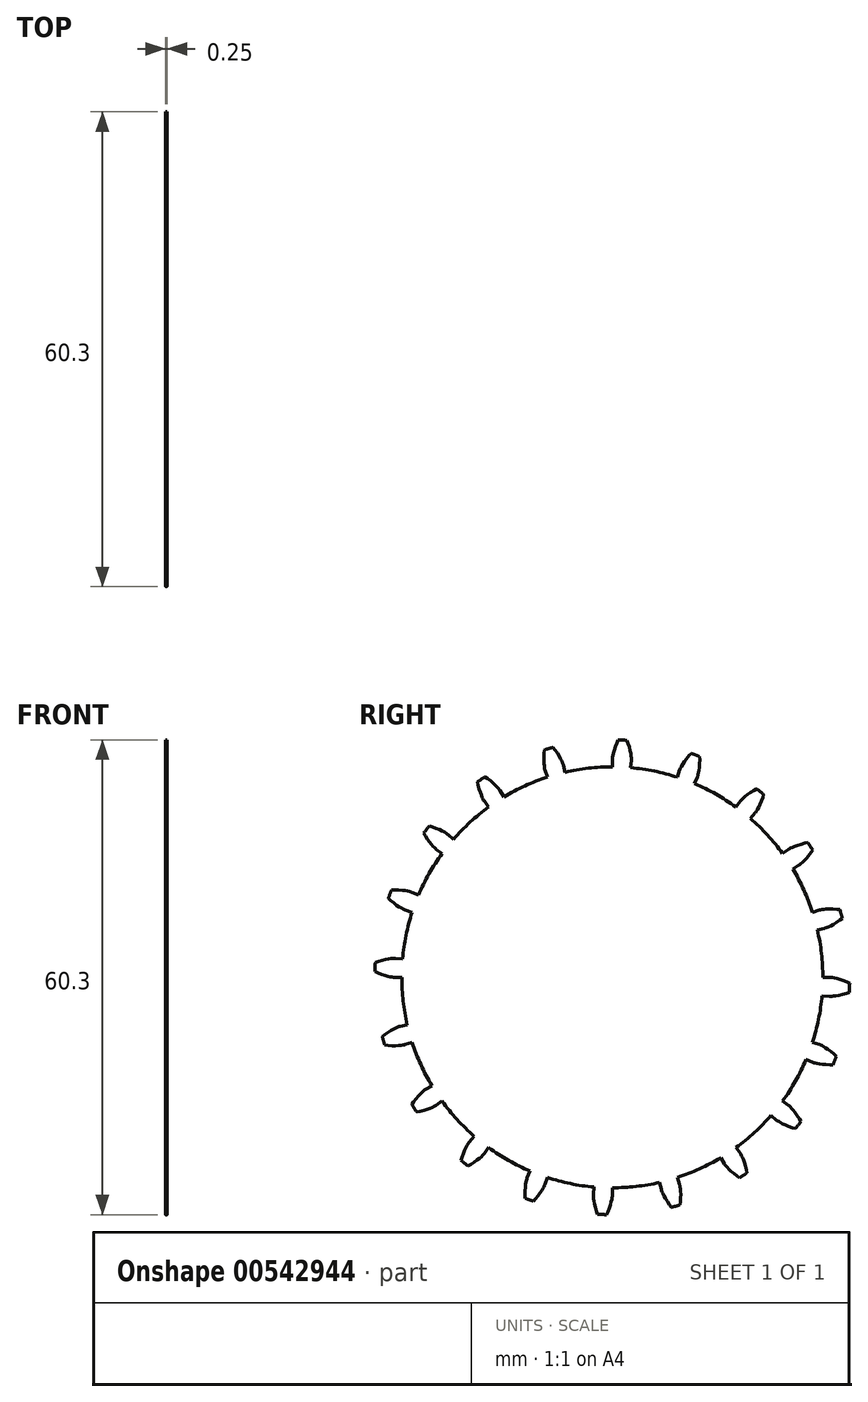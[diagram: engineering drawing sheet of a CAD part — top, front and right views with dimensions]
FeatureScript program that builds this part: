
annotation { "Feature Type Name" : "Feature", "Feature Type Description" : "" }
export const myFeature = defineFeature(function(context is Context, id is Id, definition is map)
    precondition{}
    {
        {
            assignVariable(context, id + "F0", {"name" : "GearThickness", "anyValue" : .25});
        }
        {
            var Q0;
            Q0=qCreatedBy(makeId("Right.planeOp"),FACE);
            var sketch = newSketch(context, id + "F1", { "sketchPlane" : qUnion([Q0])});
            skCircle(sketch, "E0", {"center": v(0, 0) * mm, "radius": 26.74 * mm});
            skCircle(sketch, "E1", {"center": v(0, 0) * mm, "radius": 27.66 * mm, "construction": true});
            skCircle(sketch, "E2", {"center": v(0, 0) * mm, "radius": 28.58 * mm, "construction": true});
            skCircle(sketch, "E3", {"center": v(0, 0) * mm, "radius": 30.16 * mm});
            skLineSegment(sketch, "E4", {"start": v(0, 0) * mm, "end": v(-27.66, 0) * mm, "construction": true});
            skLineSegment(sketch, "E5.1.0", {"start": v(0, 0) * mm, "end": v(-27.63, 1.38) * mm, "construction": true});
            skLineSegment(sketch, "E5.2.0", {"start": v(0, 0) * mm, "end": v(-27.53, 2.76) * mm, "construction": true});
            skLineSegment(sketch, "E5.3.0", {"start": v(0, 0) * mm, "end": v(-27.35, 4.13) * mm, "construction": true});
            skLineSegment(sketch, "E5.4.0", {"start": v(0, 0) * mm, "end": v(-27.11, 5.5) * mm, "construction": true});
            skLineSegment(sketch, "E5.5.0", {"start": v(0, 0) * mm, "end": v(-26.8, 6.84) * mm, "construction": true});
            skLineSegment(sketch, "E5.6.0", {"start": v(0, 0) * mm, "end": v(-26.43, 8.18) * mm, "construction": true});
            skLineSegment(sketch, "E5.7.0", {"start": v(0, 0) * mm, "end": v(-25.99, 9.49) * mm, "construction": true});
            skLineSegment(sketch, "E5.8.0", {"start": v(0, 0) * mm, "end": v(-25.48, 10.77) * mm, "construction": true});
            skLineSegment(sketch, "E5.9.0", {"start": v(0, 0) * mm, "end": v(-24.91, 12.03) * mm, "construction": true});
            skLineSegment(sketch, "E5.10.0", {"start": v(0, 0) * mm, "end": v(-24.28, 13.26) * mm, "construction": true});
            skLineSegment(sketch, "E5.11.0", {"start": v(0, 0) * mm, "end": v(-23.58, 14.46) * mm, "construction": true});
            skLineSegment(sketch, "E5.12.0", {"start": v(0, 0) * mm, "end": v(-22.83, 15.62) * mm, "construction": true});
            skLineSegment(sketch, "E5.13.0", {"start": v(0, 0) * mm, "end": v(-22.02, 16.74) * mm, "construction": true});
            skLineSegment(sketch, "E5.14.0", {"start": v(0, 0) * mm, "end": v(-21.16, 17.82) * mm, "construction": true});
            skLineSegment(sketch, "E5.anchor2", {"start": v(0, 0) * mm, "end": v(-21.16, 17.82) * mm, "construction": true});
            skLineSegment(sketch, "E6", {"start": v(-27.63, 1.38) * mm, "end": v(-27.7, 0) * mm, "construction": true});
            skLineSegment(sketch, "E7", {"start": v(-27.53, 2.76) * mm, "end": v(-27.8, 0) * mm, "construction": true});
            skLineSegment(sketch, "E8", {"start": v(-27.35, 4.13) * mm, "end": v(-27.97, 0.03) * mm, "construction": true});
            skLineSegment(sketch, "E9", {"start": v(-26.8, 6.84) * mm, "end": v(-28.52, 0.14) * mm, "construction": true});
            skLineSegment(sketch, "E10", {"start": v(-26.43, 8.18) * mm, "end": v(-28.88, 0.25) * mm, "construction": true});
            skLineSegment(sketch, "E11", {"start": v(-25.99, 9.49) * mm, "end": v(-29.3, 0.4) * mm, "construction": true});
            skLineSegment(sketch, "E12", {"start": v(-25.48, 10.77) * mm, "end": v(-29.8, 0.58) * mm, "construction": true});
            skLineSegment(sketch, "E13", {"start": v(-24.91, 12.03) * mm, "end": v(-30.33, 0.82) * mm, "construction": true});
            skLineSegment(sketch, "E14", {"start": v(-24.28, 13.26) * mm, "end": v(-30.9, 1.12) * mm, "construction": true});
            skLineSegment(sketch, "E15", {"start": v(-23.58, 14.46) * mm, "end": v(-31.54, 1.49) * mm, "construction": true});
            skLineSegment(sketch, "E16", {"start": v(-27.11, 5.5) * mm, "end": v(-28.21, 0.07) * mm, "construction": true});
            skLineSegment(sketch, "E17", {"start": v(-22.83, 15.62) * mm, "end": v(-32.2, 1.92) * mm, "construction": true});
            skLineSegment(sketch, "E18", {"start": v(-22.02, 16.74) * mm, "end": v(-32.9, 2.43) * mm, "construction": true});
            skLineSegment(sketch, "E19", {"start": v(-21.16, 17.82) * mm, "end": v(-33.63, 3.01) * mm, "construction": true});
            skLineSegment(sketch, "E20", {"start": v(0, 0) * mm, "end": v(-27.64, 1.2) * mm, "construction": true});
            skLineSegment(sketch, "E21", {"start": v(-26.74, 0) * mm, "end": v(-27.66, 0) * mm});
            skLineSegment(sketch, "E22.MirrorCS", {"start": v(-26.64, 2.33) * mm, "end": v(-27.56, 2.41) * mm});
            skLineSegment(sketch, "E23", {"start": v(-27.66, 0) * mm, "end": v(-27.7, 0) * mm});
            skLineSegment(sketch, "E24", {"start": v(-27.7, 0) * mm, "end": v(-27.8, 0) * mm});
            skLineSegment(sketch, "E25", {"start": v(-27.8, 0) * mm, "end": v(-27.97, 0.03) * mm});
            skLineSegment(sketch, "E26", {"start": v(-27.97, 0.03) * mm, "end": v(-28.21, 0.07) * mm});
            skLineSegment(sketch, "E27", {"start": v(-28.21, 0.07) * mm, "end": v(-28.52, 0.14) * mm});
            skLineSegment(sketch, "E28", {"start": v(-28.52, 0.14) * mm, "end": v(-28.88, 0.25) * mm});
            skLineSegment(sketch, "E29", {"start": v(-28.88, 0.25) * mm, "end": v(-29.3, 0.4) * mm});
            skLineSegment(sketch, "E30", {"start": v(-29.3, 0.4) * mm, "end": v(-29.8, 0.58) * mm});
            skLineSegment(sketch, "E31", {"start": v(-29.8, 0.58) * mm, "end": v(-30.33, 0.82) * mm});
            skLineSegment(sketch, "E32", {"start": v(-30.33, 0.82) * mm, "end": v(-30.9, 1.12) * mm});
            skLineSegment(sketch, "E33", {"start": v(-30.9, 1.12) * mm, "end": v(-31.54, 1.49) * mm});
            skLineSegment(sketch, "E34", {"start": v(-31.54, 1.49) * mm, "end": v(-32.2, 1.92) * mm});
            skLineSegment(sketch, "E35", {"start": v(-32.2, 1.92) * mm, "end": v(-32.9, 2.43) * mm});
            skLineSegment(sketch, "E36", {"start": v(-32.9, 2.43) * mm, "end": v(-33.63, 3.01) * mm});
            skLineSegment(sketch, "E37.MirrorCS", {"start": v(-27.56, 2.41) * mm, "end": v(-27.6, 2.41) * mm});
            skLineSegment(sketch, "E38.MirrorCS", {"start": v(-27.6, 2.41) * mm, "end": v(-27.7, 2.41) * mm});
            skLineSegment(sketch, "E39.MirrorCS", {"start": v(-27.7, 2.41) * mm, "end": v(-27.87, 2.4) * mm});
            skLineSegment(sketch, "E40.MirrorCS", {"start": v(-27.87, 2.4) * mm, "end": v(-28.11, 2.39) * mm});
            skLineSegment(sketch, "E41.MirrorCS", {"start": v(-28.42, 2.34) * mm, "end": v(-28.8, 2.27) * mm});
            skLineSegment(sketch, "E42.MirrorCS", {"start": v(-28.8, 2.27) * mm, "end": v(-29.23, 2.17) * mm});
            skLineSegment(sketch, "E43.MirrorCS", {"start": v(-29.23, 2.17) * mm, "end": v(-29.73, 2.02) * mm});
            skLineSegment(sketch, "E44.MirrorCS", {"start": v(-29.73, 2.02) * mm, "end": v(-30.28, 1.82) * mm});
            skLineSegment(sketch, "E45.MirrorCS", {"start": v(-30.9, 1.57) * mm, "end": v(-31.55, 1.27) * mm});
            skLineSegment(sketch, "E46.MirrorCS", {"start": v(-30.28, 1.82) * mm, "end": v(-30.9, 1.57) * mm});
            skLineSegment(sketch, "E47.MirrorCS", {"start": v(-31.55, 1.27) * mm, "end": v(-32.25, 0.9) * mm});
            skLineSegment(sketch, "E48.MirrorCS", {"start": v(-32.25, 0.9) * mm, "end": v(-33, 0.45) * mm});
            skLineSegment(sketch, "E49.MirrorCS", {"start": v(-33, 0.45) * mm, "end": v(-33.77, -0.07) * mm});
            skLineSegment(sketch, "E50.MirrorCS", {"start": v(-28.11, 2.39) * mm, "end": v(-28.42, 2.34) * mm});
            skLineSegment(sketch, "E51.1.0", {"start": v(-25.43, -8.26) * mm, "end": v(-26.31, -8.55) * mm});
            skLineSegment(sketch, "E51.1.1", {"start": v(-30.4, -8.54) * mm, "end": v(-30.95, -9.12) * mm});
            skLineSegment(sketch, "E51.1.2", {"start": v(-26.05, -6.01) * mm, "end": v(-26.96, -6.22) * mm});
            skLineSegment(sketch, "E51.1.3", {"start": v(-29.86, -8.05) * mm, "end": v(-30.4, -8.54) * mm});
            skLineSegment(sketch, "E51.1.4", {"start": v(-29.74, -8.48) * mm, "end": v(-30.45, -8.33) * mm});
            skLineSegment(sketch, "E51.1.5", {"start": v(-30.45, -8.33) * mm, "end": v(-31.22, -8.12) * mm});
            skLineSegment(sketch, "E51.1.6", {"start": v(-29.36, -7.62) * mm, "end": v(-29.86, -8.05) * mm});
            skLineSegment(sketch, "E51.1.7", {"start": v(-31.52, -9.77) * mm, "end": v(-32.1, -10.5) * mm});
            skLineSegment(sketch, "E51.1.8", {"start": v(-28.9, -7.27) * mm, "end": v(-29.36, -7.62) * mm});
            skLineSegment(sketch, "E51.1.9", {"start": v(-32.05, -7.86) * mm, "end": v(-32.92, -7.53) * mm});
            skLineSegment(sketch, "E51.1.10", {"start": v(-30.95, -9.12) * mm, "end": v(-31.52, -9.77) * mm});
            skLineSegment(sketch, "E51.1.11", {"start": v(-29.1, -8.59) * mm, "end": v(-29.74, -8.48) * mm});
            skLineSegment(sketch, "E51.1.12", {"start": v(-31.22, -8.12) * mm, "end": v(-32.05, -7.86) * mm});
            skLineSegment(sketch, "E51.1.13", {"start": v(-27.75, -6.55) * mm, "end": v(-28.09, -6.74) * mm});
            skLineSegment(sketch, "E51.1.14", {"start": v(-28.09, -6.74) * mm, "end": v(-28.47, -6.97) * mm});
            skLineSegment(sketch, "E51.1.15", {"start": v(-28.47, -6.97) * mm, "end": v(-28.9, -7.27) * mm});
            skLineSegment(sketch, "E51.1.16", {"start": v(-28, -8.69) * mm, "end": v(-28.51, -8.65) * mm});
            skLineSegment(sketch, "E51.1.17", {"start": v(-27.54, -8.7) * mm, "end": v(-28, -8.69) * mm});
            skLineSegment(sketch, "E51.1.18", {"start": v(-28.51, -8.65) * mm, "end": v(-29.1, -8.59) * mm});
            skLineSegment(sketch, "E51.1.19", {"start": v(-27.47, -6.42) * mm, "end": v(-27.75, -6.55) * mm});
            skLineSegment(sketch, "E51.1.20", {"start": v(-27.25, -6.32) * mm, "end": v(-27.47, -6.42) * mm});
            skLineSegment(sketch, "E51.1.21", {"start": v(-27.16, -8.68) * mm, "end": v(-27.54, -8.7) * mm});
            skLineSegment(sketch, "E51.1.22", {"start": v(-26.85, -8.65) * mm, "end": v(-27.16, -8.68) * mm});
            skLineSegment(sketch, "E51.1.23", {"start": v(-26.44, -8.58) * mm, "end": v(-26.61, -8.62) * mm});
            skLineSegment(sketch, "E51.1.24", {"start": v(-26.96, -6.22) * mm, "end": v(-26.99, -6.23) * mm});
            skLineSegment(sketch, "E51.1.25", {"start": v(-26.99, -6.23) * mm, "end": v(-27.09, -6.26) * mm});
            skLineSegment(sketch, "E51.1.26", {"start": v(-26.61, -8.62) * mm, "end": v(-26.85, -8.65) * mm});
            skLineSegment(sketch, "E51.1.27", {"start": v(-27.09, -6.26) * mm, "end": v(-27.25, -6.32) * mm});
            skLineSegment(sketch, "E51.1.28", {"start": v(-26.34, -8.56) * mm, "end": v(-26.44, -8.58) * mm});
            skLineSegment(sketch, "E51.1.29", {"start": v(-26.31, -8.55) * mm, "end": v(-26.34, -8.56) * mm});
            skLineSegment(sketch, "E51.2.0", {"start": v(-21.63, -15.72) * mm, "end": v(-22.38, -16.26) * mm});
            skLineSegment(sketch, "E51.2.1", {"start": v(-26.27, -17.52) * mm, "end": v(-26.62, -18.23) * mm});
            skLineSegment(sketch, "E51.2.2", {"start": v(-22.92, -13.77) * mm, "end": v(-23.71, -14.25) * mm});
            skLineSegment(sketch, "E51.2.3", {"start": v(-25.92, -16.88) * mm, "end": v(-26.27, -17.52) * mm});
            skLineSegment(sketch, "E51.2.4", {"start": v(-25.67, -17.26) * mm, "end": v(-26.39, -17.33) * mm});
            skLineSegment(sketch, "E51.2.5", {"start": v(-26.39, -17.33) * mm, "end": v(-27.18, -17.38) * mm});
            skLineSegment(sketch, "E51.2.6", {"start": v(-25.57, -16.32) * mm, "end": v(-25.92, -16.88) * mm});
            skLineSegment(sketch, "E51.2.7", {"start": v(-26.96, -19.03) * mm, "end": v(-27.28, -19.9) * mm});
            skLineSegment(sketch, "E51.2.8", {"start": v(-25.24, -15.84) * mm, "end": v(-25.57, -16.32) * mm});
            skLineSegment(sketch, "E51.2.9", {"start": v(-28.05, -17.38) * mm, "end": v(-28.98, -17.33) * mm});
            skLineSegment(sketch, "E51.2.10", {"start": v(-26.62, -18.23) * mm, "end": v(-26.96, -19.03) * mm});
            skLineSegment(sketch, "E51.2.11", {"start": v(-25.02, -17.16) * mm, "end": v(-25.67, -17.26) * mm});
            skLineSegment(sketch, "E51.2.12", {"start": v(-27.18, -17.38) * mm, "end": v(-28.05, -17.38) * mm});
            skLineSegment(sketch, "E51.2.13", {"start": v(-24.37, -14.8) * mm, "end": v(-24.63, -15.09) * mm});
            skLineSegment(sketch, "E51.2.14", {"start": v(-24.63, -15.09) * mm, "end": v(-24.92, -15.43) * mm});
            skLineSegment(sketch, "E51.2.15", {"start": v(-24.92, -15.43) * mm, "end": v(-25.24, -15.84) * mm});
            skLineSegment(sketch, "E51.2.16", {"start": v(-23.94, -16.91) * mm, "end": v(-24.44, -17.04) * mm});
            skLineSegment(sketch, "E51.2.17", {"start": v(-23.51, -16.78) * mm, "end": v(-23.94, -16.91) * mm});
            skLineSegment(sketch, "E51.2.18", {"start": v(-24.44, -17.04) * mm, "end": v(-25.02, -17.16) * mm});
            skLineSegment(sketch, "E51.2.19", {"start": v(-24.15, -14.6) * mm, "end": v(-24.37, -14.8) * mm});
            skLineSegment(sketch, "E51.2.20", {"start": v(-23.96, -14.43) * mm, "end": v(-24.15, -14.6) * mm});
            skLineSegment(sketch, "E51.2.21", {"start": v(-23.15, -16.65) * mm, "end": v(-23.51, -16.78) * mm});
            skLineSegment(sketch, "E51.2.22", {"start": v(-22.87, -16.52) * mm, "end": v(-23.15, -16.65) * mm});
            skLineSegment(sketch, "E51.2.23", {"start": v(-22.5, -16.33) * mm, "end": v(-22.65, -16.42) * mm});
            skLineSegment(sketch, "E51.2.24", {"start": v(-23.71, -14.25) * mm, "end": v(-23.74, -14.27) * mm});
            skLineSegment(sketch, "E51.2.25", {"start": v(-23.74, -14.27) * mm, "end": v(-23.83, -14.33) * mm});
            skLineSegment(sketch, "E51.2.26", {"start": v(-22.65, -16.42) * mm, "end": v(-22.87, -16.52) * mm});
            skLineSegment(sketch, "E51.2.27", {"start": v(-23.83, -14.33) * mm, "end": v(-23.96, -14.43) * mm});
            skLineSegment(sketch, "E51.2.28", {"start": v(-22.4, -16.28) * mm, "end": v(-22.5, -16.33) * mm});
            skLineSegment(sketch, "E51.2.29", {"start": v(-22.38, -16.26) * mm, "end": v(-22.4, -16.28) * mm});
            skLineSegment(sketch, "E51.3.0", {"start": v(-15.72, -21.63) * mm, "end": v(-16.26, -22.38) * mm});
            skLineSegment(sketch, "E51.3.1", {"start": v(-19.57, -24.78) * mm, "end": v(-19.68, -25.57) * mm});
            skLineSegment(sketch, "E51.3.2", {"start": v(-17.54, -20.18) * mm, "end": v(-18.15, -20.88) * mm});
            skLineSegment(sketch, "E51.3.3", {"start": v(-19.43, -24.07) * mm, "end": v(-19.57, -24.78) * mm});
            skLineSegment(sketch, "E51.3.4", {"start": v(-19.08, -24.35) * mm, "end": v(-19.74, -24.64) * mm});
            skLineSegment(sketch, "E51.3.5", {"start": v(-19.74, -24.64) * mm, "end": v(-20.48, -24.93) * mm});
            skLineSegment(sketch, "E51.3.6", {"start": v(-19.27, -23.43) * mm, "end": v(-19.43, -24.07) * mm});
            skLineSegment(sketch, "E51.3.7", {"start": v(-19.76, -26.43) * mm, "end": v(-19.8, -27.36) * mm});
            skLineSegment(sketch, "E51.3.8", {"start": v(-19.1, -22.86) * mm, "end": v(-19.27, -23.43) * mm});
            skLineSegment(sketch, "E51.3.9", {"start": v(-21.3, -25.2) * mm, "end": v(-22.2, -25.44) * mm});
            skLineSegment(sketch, "E51.3.10", {"start": v(-19.68, -25.57) * mm, "end": v(-19.76, -26.43) * mm});
            skLineSegment(sketch, "E51.3.11", {"start": v(-18.5, -24.05) * mm, "end": v(-19.08, -24.35) * mm});
            skLineSegment(sketch, "E51.3.12", {"start": v(-20.48, -24.93) * mm, "end": v(-21.3, -25.2) * mm});
            skLineSegment(sketch, "E51.3.13", {"start": v(-18.6, -21.62) * mm, "end": v(-18.76, -21.96) * mm});
            skLineSegment(sketch, "E51.3.14", {"start": v(-18.76, -21.96) * mm, "end": v(-18.93, -22.38) * mm});
            skLineSegment(sketch, "E51.3.15", {"start": v(-18.93, -22.38) * mm, "end": v(-19.1, -22.86) * mm});
            skLineSegment(sketch, "E51.3.16", {"start": v(-17.54, -23.48) * mm, "end": v(-17.98, -23.76) * mm});
            skLineSegment(sketch, "E51.3.17", {"start": v(-17.18, -23.22) * mm, "end": v(-17.54, -23.48) * mm});
            skLineSegment(sketch, "E51.3.18", {"start": v(-17.98, -23.76) * mm, "end": v(-18.5, -24.05) * mm});
            skLineSegment(sketch, "E51.3.19", {"start": v(-18.45, -21.34) * mm, "end": v(-18.6, -21.62) * mm});
            skLineSegment(sketch, "E51.3.20", {"start": v(-18.33, -21.13) * mm, "end": v(-18.45, -21.34) * mm});
            skLineSegment(sketch, "E51.3.21", {"start": v(-16.88, -22.99) * mm, "end": v(-17.18, -23.22) * mm});
            skLineSegment(sketch, "E51.3.22", {"start": v(-16.64, -22.78) * mm, "end": v(-16.88, -22.99) * mm});
            skLineSegment(sketch, "E51.3.23", {"start": v(-16.35, -22.49) * mm, "end": v(-16.47, -22.61) * mm});
            skLineSegment(sketch, "E51.3.24", {"start": v(-18.15, -20.88) * mm, "end": v(-18.17, -20.9) * mm});
            skLineSegment(sketch, "E51.3.25", {"start": v(-18.17, -20.9) * mm, "end": v(-18.23, -20.99) * mm});
            skLineSegment(sketch, "E51.3.26", {"start": v(-16.47, -22.61) * mm, "end": v(-16.64, -22.78) * mm});
            skLineSegment(sketch, "E51.3.27", {"start": v(-18.23, -20.99) * mm, "end": v(-18.33, -21.13) * mm});
            skLineSegment(sketch, "E51.3.28", {"start": v(-16.28, -22.4) * mm, "end": v(-16.35, -22.49) * mm});
            skLineSegment(sketch, "E51.3.29", {"start": v(-16.26, -22.38) * mm, "end": v(-16.28, -22.4) * mm});
            skLineSegment(sketch, "E51.4.0", {"start": v(-8.26, -25.43) * mm, "end": v(-8.55, -26.31) * mm});
            skLineSegment(sketch, "E51.4.1", {"start": v(-10.95, -29.61) * mm, "end": v(-10.82, -30.4) * mm});
            skLineSegment(sketch, "E51.4.2", {"start": v(-10.45, -24.61) * mm, "end": v(-10.8, -25.47) * mm});
            skLineSegment(sketch, "E51.4.3", {"start": v(-11.04, -28.9) * mm, "end": v(-10.95, -29.61) * mm});
            skLineSegment(sketch, "E51.4.4", {"start": v(-10.62, -29.05) * mm, "end": v(-11.16, -29.53) * mm});
            skLineSegment(sketch, "E51.4.5", {"start": v(-11.16, -29.53) * mm, "end": v(-11.78, -30.04) * mm});
            skLineSegment(sketch, "E51.4.6", {"start": v(-11.1, -28.24) * mm, "end": v(-11.04, -28.9) * mm});
            skLineSegment(sketch, "E51.4.7", {"start": v(-10.62, -31.24) * mm, "end": v(-10.37, -32.14) * mm});
            skLineSegment(sketch, "E51.4.8", {"start": v(-11.1, -27.65) * mm, "end": v(-11.1, -28.24) * mm});
            skLineSegment(sketch, "E51.4.9", {"start": v(-12.48, -30.55) * mm, "end": v(-13.26, -31.06) * mm});
            skLineSegment(sketch, "E51.4.10", {"start": v(-10.82, -30.4) * mm, "end": v(-10.62, -31.24) * mm});
            skLineSegment(sketch, "E51.4.11", {"start": v(-10.15, -28.59) * mm, "end": v(-10.62, -29.05) * mm});
            skLineSegment(sketch, "E51.4.12", {"start": v(-11.78, -30.04) * mm, "end": v(-12.48, -30.55) * mm});
            skLineSegment(sketch, "E51.4.13", {"start": v(-11.01, -26.3) * mm, "end": v(-11.06, -26.68) * mm});
            skLineSegment(sketch, "E51.4.14", {"start": v(-11.06, -26.68) * mm, "end": v(-11.1, -27.13) * mm});
            skLineSegment(sketch, "E51.4.15", {"start": v(-11.1, -27.13) * mm, "end": v(-11.1, -27.65) * mm});
            skLineSegment(sketch, "E51.4.16", {"start": v(-9.43, -27.75) * mm, "end": v(-9.76, -28.15) * mm});
            skLineSegment(sketch, "E51.4.17", {"start": v(-9.16, -27.4) * mm, "end": v(-9.43, -27.75) * mm});
            skLineSegment(sketch, "E51.4.18", {"start": v(-9.76, -28.15) * mm, "end": v(-10.15, -28.59) * mm});
            skLineSegment(sketch, "E51.4.19", {"start": v(-10.96, -26) * mm, "end": v(-11.01, -26.3) * mm});
            skLineSegment(sketch, "E51.4.20", {"start": v(-10.9, -25.76) * mm, "end": v(-10.96, -26) * mm});
            skLineSegment(sketch, "E51.4.21", {"start": v(-8.95, -27.08) * mm, "end": v(-9.16, -27.4) * mm});
            skLineSegment(sketch, "E51.4.22", {"start": v(-8.79, -26.8) * mm, "end": v(-8.95, -27.08) * mm});
            skLineSegment(sketch, "E51.4.23", {"start": v(-8.6, -26.44) * mm, "end": v(-8.67, -26.6) * mm});
            skLineSegment(sketch, "E51.4.24", {"start": v(-10.8, -25.47) * mm, "end": v(-10.82, -25.5) * mm});
            skLineSegment(sketch, "E51.4.25", {"start": v(-10.82, -25.5) * mm, "end": v(-10.85, -25.6) * mm});
            skLineSegment(sketch, "E51.4.26", {"start": v(-8.67, -26.6) * mm, "end": v(-8.79, -26.8) * mm});
            skLineSegment(sketch, "E51.4.27", {"start": v(-10.85, -25.6) * mm, "end": v(-10.9, -25.76) * mm});
            skLineSegment(sketch, "E51.4.28", {"start": v(-8.56, -26.34) * mm, "end": v(-8.6, -26.44) * mm});
            skLineSegment(sketch, "E51.4.29", {"start": v(-8.55, -26.31) * mm, "end": v(-8.56, -26.34) * mm});
            skLineSegment(sketch, "E51.5.0", {"start": v(0, -26.74) * mm, "end": v(0, -27.66) * mm});
            skLineSegment(sketch, "E51.5.1", {"start": v(-1.27, -31.55) * mm, "end": v(-0.9, -32.25) * mm});
            skLineSegment(sketch, "E51.5.2", {"start": v(-2.33, -26.64) * mm, "end": v(-2.41, -27.56) * mm});
            skLineSegment(sketch, "E51.5.3", {"start": v(-1.57, -30.9) * mm, "end": v(-1.27, -31.55) * mm});
            skLineSegment(sketch, "E51.5.4", {"start": v(-1.12, -30.9) * mm, "end": v(-1.49, -31.54) * mm});
            skLineSegment(sketch, "E51.5.5", {"start": v(-1.49, -31.54) * mm, "end": v(-1.92, -32.2) * mm});
            skLineSegment(sketch, "E51.5.6", {"start": v(-1.82, -30.28) * mm, "end": v(-1.57, -30.9) * mm});
            skLineSegment(sketch, "E51.5.7", {"start": v(-0.45, -33) * mm, "end": v(0.07, -33.77) * mm});
            skLineSegment(sketch, "E51.5.8", {"start": v(-2.02, -29.73) * mm, "end": v(-1.82, -30.28) * mm});
            skLineSegment(sketch, "E51.5.9", {"start": v(-2.43, -32.9) * mm, "end": v(-3.01, -33.63) * mm});
            skLineSegment(sketch, "E51.5.10", {"start": v(-0.9, -32.25) * mm, "end": v(-0.45, -33) * mm});
            skLineSegment(sketch, "E51.5.11", {"start": v(-0.82, -30.33) * mm, "end": v(-1.12, -30.9) * mm});
            skLineSegment(sketch, "E51.5.12", {"start": v(-1.92, -32.2) * mm, "end": v(-2.43, -32.9) * mm});
            skLineSegment(sketch, "E51.5.13", {"start": v(-2.34, -28.42) * mm, "end": v(-2.27, -28.8) * mm});
            skLineSegment(sketch, "E51.5.14", {"start": v(-2.27, -28.8) * mm, "end": v(-2.17, -29.23) * mm});
            skLineSegment(sketch, "E51.5.15", {"start": v(-2.17, -29.23) * mm, "end": v(-2.02, -29.73) * mm});
            skLineSegment(sketch, "E51.5.16", {"start": v(-0.4, -29.3) * mm, "end": v(-0.58, -29.8) * mm});
            skLineSegment(sketch, "E51.5.17", {"start": v(-0.25, -28.88) * mm, "end": v(-0.4, -29.3) * mm});
            skLineSegment(sketch, "E51.5.18", {"start": v(-0.58, -29.8) * mm, "end": v(-0.82, -30.33) * mm});
            skLineSegment(sketch, "E51.5.19", {"start": v(-2.39, -28.11) * mm, "end": v(-2.34, -28.42) * mm});
            skLineSegment(sketch, "E51.5.20", {"start": v(-2.4, -27.87) * mm, "end": v(-2.39, -28.11) * mm});
            skLineSegment(sketch, "E51.5.21", {"start": v(-0.14, -28.52) * mm, "end": v(-0.25, -28.88) * mm});
            skLineSegment(sketch, "E51.5.22", {"start": v(-0.07, -28.21) * mm, "end": v(-0.14, -28.52) * mm});
            skLineSegment(sketch, "E51.5.23", {"start": v(0, -27.8) * mm, "end": v(-0.03, -27.97) * mm});
            skLineSegment(sketch, "E51.5.24", {"start": v(-2.41, -27.56) * mm, "end": v(-2.41, -27.6) * mm});
            skLineSegment(sketch, "E51.5.25", {"start": v(-2.41, -27.6) * mm, "end": v(-2.41, -27.7) * mm});
            skLineSegment(sketch, "E51.5.26", {"start": v(-0.03, -27.97) * mm, "end": v(-0.07, -28.21) * mm});
            skLineSegment(sketch, "E51.5.27", {"start": v(-2.41, -27.7) * mm, "end": v(-2.4, -27.87) * mm});
            skLineSegment(sketch, "E51.5.28", {"start": v(0, -27.7) * mm, "end": v(0, -27.8) * mm});
            skLineSegment(sketch, "E51.5.29", {"start": v(0, -27.66) * mm, "end": v(0, -27.7) * mm});
            skLineSegment(sketch, "E51.6.0", {"start": v(8.26, -25.43) * mm, "end": v(8.55, -26.31) * mm});
            skLineSegment(sketch, "E51.6.1", {"start": v(8.54, -30.4) * mm, "end": v(9.12, -30.95) * mm});
            skLineSegment(sketch, "E51.6.2", {"start": v(6.01, -26.05) * mm, "end": v(6.22, -26.96) * mm});
            skLineSegment(sketch, "E51.6.3", {"start": v(8.05, -29.86) * mm, "end": v(8.54, -30.4) * mm});
            skLineSegment(sketch, "E51.6.4", {"start": v(8.48, -29.74) * mm, "end": v(8.33, -30.45) * mm});
            skLineSegment(sketch, "E51.6.5", {"start": v(8.33, -30.45) * mm, "end": v(8.12, -31.22) * mm});
            skLineSegment(sketch, "E51.6.6", {"start": v(7.62, -29.36) * mm, "end": v(8.05, -29.86) * mm});
            skLineSegment(sketch, "E51.6.7", {"start": v(9.77, -31.52) * mm, "end": v(10.5, -32.1) * mm});
            skLineSegment(sketch, "E51.6.8", {"start": v(7.27, -28.9) * mm, "end": v(7.62, -29.36) * mm});
            skLineSegment(sketch, "E51.6.9", {"start": v(7.86, -32.05) * mm, "end": v(7.53, -32.92) * mm});
            skLineSegment(sketch, "E51.6.10", {"start": v(9.12, -30.95) * mm, "end": v(9.77, -31.52) * mm});
            skLineSegment(sketch, "E51.6.11", {"start": v(8.59, -29.1) * mm, "end": v(8.48, -29.74) * mm});
            skLineSegment(sketch, "E51.6.12", {"start": v(8.12, -31.22) * mm, "end": v(7.86, -32.05) * mm});
            skLineSegment(sketch, "E51.6.13", {"start": v(6.55, -27.75) * mm, "end": v(6.74, -28.09) * mm});
            skLineSegment(sketch, "E51.6.14", {"start": v(6.74, -28.09) * mm, "end": v(6.97, -28.47) * mm});
            skLineSegment(sketch, "E51.6.15", {"start": v(6.97, -28.47) * mm, "end": v(7.27, -28.9) * mm});
            skLineSegment(sketch, "E51.6.16", {"start": v(8.69, -28) * mm, "end": v(8.65, -28.51) * mm});
            skLineSegment(sketch, "E51.6.17", {"start": v(8.7, -27.54) * mm, "end": v(8.69, -28) * mm});
            skLineSegment(sketch, "E51.6.18", {"start": v(8.65, -28.51) * mm, "end": v(8.59, -29.1) * mm});
            skLineSegment(sketch, "E51.6.19", {"start": v(6.42, -27.47) * mm, "end": v(6.55, -27.75) * mm});
            skLineSegment(sketch, "E51.6.20", {"start": v(6.32, -27.25) * mm, "end": v(6.42, -27.47) * mm});
            skLineSegment(sketch, "E51.6.21", {"start": v(8.68, -27.16) * mm, "end": v(8.7, -27.54) * mm});
            skLineSegment(sketch, "E51.6.22", {"start": v(8.65, -26.85) * mm, "end": v(8.68, -27.16) * mm});
            skLineSegment(sketch, "E51.6.23", {"start": v(8.58, -26.44) * mm, "end": v(8.62, -26.61) * mm});
            skLineSegment(sketch, "E51.6.24", {"start": v(6.22, -26.96) * mm, "end": v(6.23, -26.99) * mm});
            skLineSegment(sketch, "E51.6.25", {"start": v(6.23, -26.99) * mm, "end": v(6.26, -27.09) * mm});
            skLineSegment(sketch, "E51.6.26", {"start": v(8.62, -26.61) * mm, "end": v(8.65, -26.85) * mm});
            skLineSegment(sketch, "E51.6.27", {"start": v(6.26, -27.09) * mm, "end": v(6.32, -27.25) * mm});
            skLineSegment(sketch, "E51.6.28", {"start": v(8.56, -26.34) * mm, "end": v(8.58, -26.44) * mm});
            skLineSegment(sketch, "E51.6.29", {"start": v(8.55, -26.31) * mm, "end": v(8.56, -26.34) * mm});
            skLineSegment(sketch, "E51.7.0", {"start": v(15.72, -21.63) * mm, "end": v(16.26, -22.38) * mm});
            skLineSegment(sketch, "E51.7.1", {"start": v(17.52, -26.27) * mm, "end": v(18.23, -26.62) * mm});
            skLineSegment(sketch, "E51.7.2", {"start": v(13.77, -22.92) * mm, "end": v(14.25, -23.71) * mm});
            skLineSegment(sketch, "E51.7.3", {"start": v(16.88, -25.92) * mm, "end": v(17.52, -26.27) * mm});
            skLineSegment(sketch, "E51.7.4", {"start": v(17.26, -25.67) * mm, "end": v(17.33, -26.39) * mm});
            skLineSegment(sketch, "E51.7.5", {"start": v(17.33, -26.39) * mm, "end": v(17.38, -27.18) * mm});
            skLineSegment(sketch, "E51.7.6", {"start": v(16.32, -25.57) * mm, "end": v(16.88, -25.92) * mm});
            skLineSegment(sketch, "E51.7.7", {"start": v(19.03, -26.96) * mm, "end": v(19.9, -27.28) * mm});
            skLineSegment(sketch, "E51.7.8", {"start": v(15.84, -25.24) * mm, "end": v(16.32, -25.57) * mm});
            skLineSegment(sketch, "E51.7.9", {"start": v(17.38, -28.05) * mm, "end": v(17.33, -28.98) * mm});
            skLineSegment(sketch, "E51.7.10", {"start": v(18.23, -26.62) * mm, "end": v(19.03, -26.96) * mm});
            skLineSegment(sketch, "E51.7.11", {"start": v(17.16, -25.02) * mm, "end": v(17.26, -25.67) * mm});
            skLineSegment(sketch, "E51.7.12", {"start": v(17.38, -27.18) * mm, "end": v(17.38, -28.05) * mm});
            skLineSegment(sketch, "E51.7.13", {"start": v(14.8, -24.37) * mm, "end": v(15.09, -24.63) * mm});
            skLineSegment(sketch, "E51.7.14", {"start": v(15.09, -24.63) * mm, "end": v(15.43, -24.92) * mm});
            skLineSegment(sketch, "E51.7.15", {"start": v(15.43, -24.92) * mm, "end": v(15.84, -25.24) * mm});
            skLineSegment(sketch, "E51.7.16", {"start": v(16.91, -23.94) * mm, "end": v(17.04, -24.44) * mm});
            skLineSegment(sketch, "E51.7.17", {"start": v(16.78, -23.51) * mm, "end": v(16.91, -23.94) * mm});
            skLineSegment(sketch, "E51.7.18", {"start": v(17.04, -24.44) * mm, "end": v(17.16, -25.02) * mm});
            skLineSegment(sketch, "E51.7.19", {"start": v(14.6, -24.15) * mm, "end": v(14.8, -24.37) * mm});
            skLineSegment(sketch, "E51.7.20", {"start": v(14.43, -23.96) * mm, "end": v(14.6, -24.15) * mm});
            skLineSegment(sketch, "E51.7.21", {"start": v(16.65, -23.15) * mm, "end": v(16.78, -23.51) * mm});
            skLineSegment(sketch, "E51.7.22", {"start": v(16.52, -22.87) * mm, "end": v(16.65, -23.15) * mm});
            skLineSegment(sketch, "E51.7.23", {"start": v(16.33, -22.5) * mm, "end": v(16.42, -22.65) * mm});
            skLineSegment(sketch, "E51.7.24", {"start": v(14.25, -23.71) * mm, "end": v(14.27, -23.74) * mm});
            skLineSegment(sketch, "E51.7.25", {"start": v(14.27, -23.74) * mm, "end": v(14.33, -23.83) * mm});
            skLineSegment(sketch, "E51.7.26", {"start": v(16.42, -22.65) * mm, "end": v(16.52, -22.87) * mm});
            skLineSegment(sketch, "E51.7.27", {"start": v(14.33, -23.83) * mm, "end": v(14.43, -23.96) * mm});
            skLineSegment(sketch, "E51.7.28", {"start": v(16.28, -22.4) * mm, "end": v(16.33, -22.5) * mm});
            skLineSegment(sketch, "E51.7.29", {"start": v(16.26, -22.38) * mm, "end": v(16.28, -22.4) * mm});
            skLineSegment(sketch, "E51.8.0", {"start": v(21.63, -15.72) * mm, "end": v(22.38, -16.26) * mm});
            skLineSegment(sketch, "E51.8.1", {"start": v(24.78, -19.57) * mm, "end": v(25.57, -19.68) * mm});
            skLineSegment(sketch, "E51.8.2", {"start": v(20.18, -17.54) * mm, "end": v(20.88, -18.15) * mm});
            skLineSegment(sketch, "E51.8.3", {"start": v(24.07, -19.43) * mm, "end": v(24.78, -19.57) * mm});
            skLineSegment(sketch, "E51.8.4", {"start": v(24.35, -19.08) * mm, "end": v(24.64, -19.74) * mm});
            skLineSegment(sketch, "E51.8.5", {"start": v(24.64, -19.74) * mm, "end": v(24.93, -20.48) * mm});
            skLineSegment(sketch, "E51.8.6", {"start": v(23.43, -19.27) * mm, "end": v(24.07, -19.43) * mm});
            skLineSegment(sketch, "E51.8.7", {"start": v(26.43, -19.76) * mm, "end": v(27.36, -19.8) * mm});
            skLineSegment(sketch, "E51.8.8", {"start": v(22.86, -19.1) * mm, "end": v(23.43, -19.27) * mm});
            skLineSegment(sketch, "E51.8.9", {"start": v(25.2, -21.3) * mm, "end": v(25.44, -22.2) * mm});
            skLineSegment(sketch, "E51.8.10", {"start": v(25.57, -19.68) * mm, "end": v(26.43, -19.76) * mm});
            skLineSegment(sketch, "E51.8.11", {"start": v(24.05, -18.5) * mm, "end": v(24.35, -19.08) * mm});
            skLineSegment(sketch, "E51.8.12", {"start": v(24.93, -20.48) * mm, "end": v(25.2, -21.3) * mm});
            skLineSegment(sketch, "E51.8.13", {"start": v(21.62, -18.6) * mm, "end": v(21.96, -18.76) * mm});
            skLineSegment(sketch, "E51.8.14", {"start": v(21.96, -18.76) * mm, "end": v(22.38, -18.93) * mm});
            skLineSegment(sketch, "E51.8.15", {"start": v(22.38, -18.93) * mm, "end": v(22.86, -19.1) * mm});
            skLineSegment(sketch, "E51.8.16", {"start": v(23.48, -17.54) * mm, "end": v(23.76, -17.98) * mm});
            skLineSegment(sketch, "E51.8.17", {"start": v(23.22, -17.18) * mm, "end": v(23.48, -17.54) * mm});
            skLineSegment(sketch, "E51.8.18", {"start": v(23.76, -17.98) * mm, "end": v(24.05, -18.5) * mm});
            skLineSegment(sketch, "E51.8.19", {"start": v(21.34, -18.45) * mm, "end": v(21.62, -18.6) * mm});
            skLineSegment(sketch, "E51.8.20", {"start": v(21.13, -18.33) * mm, "end": v(21.34, -18.45) * mm});
            skLineSegment(sketch, "E51.8.21", {"start": v(22.99, -16.88) * mm, "end": v(23.22, -17.18) * mm});
            skLineSegment(sketch, "E51.8.22", {"start": v(22.78, -16.64) * mm, "end": v(22.99, -16.88) * mm});
            skLineSegment(sketch, "E51.8.23", {"start": v(22.49, -16.35) * mm, "end": v(22.61, -16.47) * mm});
            skLineSegment(sketch, "E51.8.24", {"start": v(20.88, -18.15) * mm, "end": v(20.9, -18.17) * mm});
            skLineSegment(sketch, "E51.8.25", {"start": v(20.9, -18.17) * mm, "end": v(20.99, -18.23) * mm});
            skLineSegment(sketch, "E51.8.26", {"start": v(22.61, -16.47) * mm, "end": v(22.78, -16.64) * mm});
            skLineSegment(sketch, "E51.8.27", {"start": v(20.99, -18.23) * mm, "end": v(21.13, -18.33) * mm});
            skLineSegment(sketch, "E51.8.28", {"start": v(22.4, -16.28) * mm, "end": v(22.49, -16.35) * mm});
            skLineSegment(sketch, "E51.8.29", {"start": v(22.38, -16.26) * mm, "end": v(22.4, -16.28) * mm});
            skLineSegment(sketch, "E51.9.0", {"start": v(25.43, -8.26) * mm, "end": v(26.31, -8.55) * mm});
            skLineSegment(sketch, "E51.9.1", {"start": v(29.61, -10.95) * mm, "end": v(30.4, -10.82) * mm});
            skLineSegment(sketch, "E51.9.2", {"start": v(24.61, -10.45) * mm, "end": v(25.47, -10.8) * mm});
            skLineSegment(sketch, "E51.9.3", {"start": v(28.9, -11.04) * mm, "end": v(29.61, -10.95) * mm});
            skLineSegment(sketch, "E51.9.4", {"start": v(29.05, -10.62) * mm, "end": v(29.53, -11.16) * mm});
            skLineSegment(sketch, "E51.9.5", {"start": v(29.53, -11.16) * mm, "end": v(30.04, -11.78) * mm});
            skLineSegment(sketch, "E51.9.6", {"start": v(28.24, -11.1) * mm, "end": v(28.9, -11.04) * mm});
            skLineSegment(sketch, "E51.9.7", {"start": v(31.24, -10.62) * mm, "end": v(32.14, -10.37) * mm});
            skLineSegment(sketch, "E51.9.8", {"start": v(27.65, -11.1) * mm, "end": v(28.24, -11.1) * mm});
            skLineSegment(sketch, "E51.9.9", {"start": v(30.55, -12.48) * mm, "end": v(31.06, -13.26) * mm});
            skLineSegment(sketch, "E51.9.10", {"start": v(30.4, -10.82) * mm, "end": v(31.24, -10.62) * mm});
            skLineSegment(sketch, "E51.9.11", {"start": v(28.59, -10.15) * mm, "end": v(29.05, -10.62) * mm});
            skLineSegment(sketch, "E51.9.12", {"start": v(30.04, -11.78) * mm, "end": v(30.55, -12.48) * mm});
            skLineSegment(sketch, "E51.9.13", {"start": v(26.3, -11.01) * mm, "end": v(26.68, -11.06) * mm});
            skLineSegment(sketch, "E51.9.14", {"start": v(26.68, -11.06) * mm, "end": v(27.13, -11.1) * mm});
            skLineSegment(sketch, "E51.9.15", {"start": v(27.13, -11.1) * mm, "end": v(27.65, -11.1) * mm});
            skLineSegment(sketch, "E51.9.16", {"start": v(27.75, -9.43) * mm, "end": v(28.15, -9.76) * mm});
            skLineSegment(sketch, "E51.9.17", {"start": v(27.4, -9.16) * mm, "end": v(27.75, -9.43) * mm});
            skLineSegment(sketch, "E51.9.18", {"start": v(28.15, -9.76) * mm, "end": v(28.59, -10.15) * mm});
            skLineSegment(sketch, "E51.9.19", {"start": v(26, -10.96) * mm, "end": v(26.3, -11.01) * mm});
            skLineSegment(sketch, "E51.9.20", {"start": v(25.76, -10.9) * mm, "end": v(26, -10.96) * mm});
            skLineSegment(sketch, "E51.9.21", {"start": v(27.08, -8.95) * mm, "end": v(27.4, -9.16) * mm});
            skLineSegment(sketch, "E51.9.22", {"start": v(26.8, -8.79) * mm, "end": v(27.08, -8.95) * mm});
            skLineSegment(sketch, "E51.9.23", {"start": v(26.44, -8.6) * mm, "end": v(26.6, -8.67) * mm});
            skLineSegment(sketch, "E51.9.24", {"start": v(25.47, -10.8) * mm, "end": v(25.5, -10.82) * mm});
            skLineSegment(sketch, "E51.9.25", {"start": v(25.5, -10.82) * mm, "end": v(25.6, -10.85) * mm});
            skLineSegment(sketch, "E51.9.26", {"start": v(26.6, -8.67) * mm, "end": v(26.8, -8.79) * mm});
            skLineSegment(sketch, "E51.9.27", {"start": v(25.6, -10.85) * mm, "end": v(25.76, -10.9) * mm});
            skLineSegment(sketch, "E51.9.28", {"start": v(26.34, -8.56) * mm, "end": v(26.44, -8.6) * mm});
            skLineSegment(sketch, "E51.9.29", {"start": v(26.31, -8.55) * mm, "end": v(26.34, -8.56) * mm});
            skLineSegment(sketch, "E51.10.0", {"start": v(26.74, 0) * mm, "end": v(27.66, 0) * mm});
            skLineSegment(sketch, "E51.10.1", {"start": v(31.55, -1.27) * mm, "end": v(32.25, -0.9) * mm});
            skLineSegment(sketch, "E51.10.2", {"start": v(26.64, -2.33) * mm, "end": v(27.56, -2.41) * mm});
            skLineSegment(sketch, "E51.10.3", {"start": v(30.9, -1.57) * mm, "end": v(31.55, -1.27) * mm});
            skLineSegment(sketch, "E51.10.4", {"start": v(30.9, -1.12) * mm, "end": v(31.54, -1.49) * mm});
            skLineSegment(sketch, "E51.10.5", {"start": v(31.54, -1.49) * mm, "end": v(32.2, -1.92) * mm});
            skLineSegment(sketch, "E51.10.6", {"start": v(30.28, -1.82) * mm, "end": v(30.9, -1.57) * mm});
            skLineSegment(sketch, "E51.10.7", {"start": v(33, -0.45) * mm, "end": v(33.77, 0.07) * mm});
            skLineSegment(sketch, "E51.10.8", {"start": v(29.73, -2.02) * mm, "end": v(30.28, -1.82) * mm});
            skLineSegment(sketch, "E51.10.9", {"start": v(32.9, -2.43) * mm, "end": v(33.63, -3.01) * mm});
            skLineSegment(sketch, "E51.10.10", {"start": v(32.25, -0.9) * mm, "end": v(33, -0.45) * mm});
            skLineSegment(sketch, "E51.10.11", {"start": v(30.33, -0.82) * mm, "end": v(30.9, -1.12) * mm});
            skLineSegment(sketch, "E51.10.12", {"start": v(32.2, -1.92) * mm, "end": v(32.9, -2.43) * mm});
            skLineSegment(sketch, "E51.10.13", {"start": v(28.42, -2.34) * mm, "end": v(28.8, -2.27) * mm});
            skLineSegment(sketch, "E51.10.14", {"start": v(28.8, -2.27) * mm, "end": v(29.23, -2.17) * mm});
            skLineSegment(sketch, "E51.10.15", {"start": v(29.23, -2.17) * mm, "end": v(29.73, -2.02) * mm});
            skLineSegment(sketch, "E51.10.16", {"start": v(29.3, -0.4) * mm, "end": v(29.8, -0.58) * mm});
            skLineSegment(sketch, "E51.10.17", {"start": v(28.88, -0.25) * mm, "end": v(29.3, -0.4) * mm});
            skLineSegment(sketch, "E51.10.18", {"start": v(29.8, -0.58) * mm, "end": v(30.33, -0.82) * mm});
            skLineSegment(sketch, "E51.10.19", {"start": v(28.11, -2.39) * mm, "end": v(28.42, -2.34) * mm});
            skLineSegment(sketch, "E51.10.20", {"start": v(27.87, -2.4) * mm, "end": v(28.11, -2.39) * mm});
            skLineSegment(sketch, "E51.10.21", {"start": v(28.52, -0.14) * mm, "end": v(28.88, -0.25) * mm});
            skLineSegment(sketch, "E51.10.22", {"start": v(28.21, -0.07) * mm, "end": v(28.52, -0.14) * mm});
            skLineSegment(sketch, "E51.10.23", {"start": v(27.8, 0) * mm, "end": v(27.97, -0.03) * mm});
            skLineSegment(sketch, "E51.10.24", {"start": v(27.56, -2.41) * mm, "end": v(27.6, -2.41) * mm});
            skLineSegment(sketch, "E51.10.25", {"start": v(27.6, -2.41) * mm, "end": v(27.7, -2.41) * mm});
            skLineSegment(sketch, "E51.10.26", {"start": v(27.97, -0.03) * mm, "end": v(28.21, -0.07) * mm});
            skLineSegment(sketch, "E51.10.27", {"start": v(27.7, -2.41) * mm, "end": v(27.87, -2.4) * mm});
            skLineSegment(sketch, "E51.10.28", {"start": v(27.7, 0) * mm, "end": v(27.8, 0) * mm});
            skLineSegment(sketch, "E51.10.29", {"start": v(27.66, 0) * mm, "end": v(27.7, 0) * mm});
            skLineSegment(sketch, "E51.11.0", {"start": v(25.43, 8.26) * mm, "end": v(26.31, 8.55) * mm});
            skLineSegment(sketch, "E51.11.1", {"start": v(30.4, 8.54) * mm, "end": v(30.95, 9.12) * mm});
            skLineSegment(sketch, "E51.11.2", {"start": v(26.05, 6.01) * mm, "end": v(26.96, 6.22) * mm});
            skLineSegment(sketch, "E51.11.3", {"start": v(29.86, 8.05) * mm, "end": v(30.4, 8.54) * mm});
            skLineSegment(sketch, "E51.11.4", {"start": v(29.74, 8.48) * mm, "end": v(30.45, 8.33) * mm});
            skLineSegment(sketch, "E51.11.5", {"start": v(30.45, 8.33) * mm, "end": v(31.22, 8.12) * mm});
            skLineSegment(sketch, "E51.11.6", {"start": v(29.36, 7.62) * mm, "end": v(29.86, 8.05) * mm});
            skLineSegment(sketch, "E51.11.7", {"start": v(31.52, 9.77) * mm, "end": v(32.1, 10.5) * mm});
            skLineSegment(sketch, "E51.11.8", {"start": v(28.9, 7.27) * mm, "end": v(29.36, 7.62) * mm});
            skLineSegment(sketch, "E51.11.9", {"start": v(32.05, 7.86) * mm, "end": v(32.92, 7.53) * mm});
            skLineSegment(sketch, "E51.11.10", {"start": v(30.95, 9.12) * mm, "end": v(31.52, 9.77) * mm});
            skLineSegment(sketch, "E51.11.11", {"start": v(29.1, 8.59) * mm, "end": v(29.74, 8.48) * mm});
            skLineSegment(sketch, "E51.11.12", {"start": v(31.22, 8.12) * mm, "end": v(32.05, 7.86) * mm});
            skLineSegment(sketch, "E51.11.13", {"start": v(27.75, 6.55) * mm, "end": v(28.09, 6.74) * mm});
            skLineSegment(sketch, "E51.11.14", {"start": v(28.09, 6.74) * mm, "end": v(28.47, 6.97) * mm});
            skLineSegment(sketch, "E51.11.15", {"start": v(28.47, 6.97) * mm, "end": v(28.9, 7.27) * mm});
            skLineSegment(sketch, "E51.11.16", {"start": v(28, 8.69) * mm, "end": v(28.51, 8.65) * mm});
            skLineSegment(sketch, "E51.11.17", {"start": v(27.54, 8.7) * mm, "end": v(28, 8.69) * mm});
            skLineSegment(sketch, "E51.11.18", {"start": v(28.51, 8.65) * mm, "end": v(29.1, 8.59) * mm});
            skLineSegment(sketch, "E51.11.19", {"start": v(27.47, 6.42) * mm, "end": v(27.75, 6.55) * mm});
            skLineSegment(sketch, "E51.11.20", {"start": v(27.25, 6.32) * mm, "end": v(27.47, 6.42) * mm});
            skLineSegment(sketch, "E51.11.21", {"start": v(27.16, 8.68) * mm, "end": v(27.54, 8.7) * mm});
            skLineSegment(sketch, "E51.11.22", {"start": v(26.85, 8.65) * mm, "end": v(27.16, 8.68) * mm});
            skLineSegment(sketch, "E51.11.23", {"start": v(26.44, 8.58) * mm, "end": v(26.61, 8.62) * mm});
            skLineSegment(sketch, "E51.11.24", {"start": v(26.96, 6.22) * mm, "end": v(26.99, 6.23) * mm});
            skLineSegment(sketch, "E51.11.25", {"start": v(26.99, 6.23) * mm, "end": v(27.09, 6.26) * mm});
            skLineSegment(sketch, "E51.11.26", {"start": v(26.61, 8.62) * mm, "end": v(26.85, 8.65) * mm});
            skLineSegment(sketch, "E51.11.27", {"start": v(27.09, 6.26) * mm, "end": v(27.25, 6.32) * mm});
            skLineSegment(sketch, "E51.11.28", {"start": v(26.34, 8.56) * mm, "end": v(26.44, 8.58) * mm});
            skLineSegment(sketch, "E51.11.29", {"start": v(26.31, 8.55) * mm, "end": v(26.34, 8.56) * mm});
            skLineSegment(sketch, "E51.12.0", {"start": v(21.63, 15.72) * mm, "end": v(22.38, 16.26) * mm});
            skLineSegment(sketch, "E51.12.1", {"start": v(26.27, 17.52) * mm, "end": v(26.62, 18.23) * mm});
            skLineSegment(sketch, "E51.12.2", {"start": v(22.92, 13.77) * mm, "end": v(23.71, 14.25) * mm});
            skLineSegment(sketch, "E51.12.3", {"start": v(25.92, 16.88) * mm, "end": v(26.27, 17.52) * mm});
            skLineSegment(sketch, "E51.12.4", {"start": v(25.67, 17.26) * mm, "end": v(26.39, 17.33) * mm});
            skLineSegment(sketch, "E51.12.5", {"start": v(26.39, 17.33) * mm, "end": v(27.18, 17.38) * mm});
            skLineSegment(sketch, "E51.12.6", {"start": v(25.57, 16.32) * mm, "end": v(25.92, 16.88) * mm});
            skLineSegment(sketch, "E51.12.7", {"start": v(26.96, 19.03) * mm, "end": v(27.28, 19.9) * mm});
            skLineSegment(sketch, "E51.12.8", {"start": v(25.24, 15.84) * mm, "end": v(25.57, 16.32) * mm});
            skLineSegment(sketch, "E51.12.9", {"start": v(28.05, 17.38) * mm, "end": v(28.98, 17.33) * mm});
            skLineSegment(sketch, "E51.12.10", {"start": v(26.62, 18.23) * mm, "end": v(26.96, 19.03) * mm});
            skLineSegment(sketch, "E51.12.11", {"start": v(25.02, 17.16) * mm, "end": v(25.67, 17.26) * mm});
            skLineSegment(sketch, "E51.12.12", {"start": v(27.18, 17.38) * mm, "end": v(28.05, 17.38) * mm});
            skLineSegment(sketch, "E51.12.13", {"start": v(24.37, 14.8) * mm, "end": v(24.63, 15.09) * mm});
            skLineSegment(sketch, "E51.12.14", {"start": v(24.63, 15.09) * mm, "end": v(24.92, 15.43) * mm});
            skLineSegment(sketch, "E51.12.15", {"start": v(24.92, 15.43) * mm, "end": v(25.24, 15.84) * mm});
            skLineSegment(sketch, "E51.12.16", {"start": v(23.94, 16.91) * mm, "end": v(24.44, 17.04) * mm});
            skLineSegment(sketch, "E51.12.17", {"start": v(23.51, 16.78) * mm, "end": v(23.94, 16.91) * mm});
            skLineSegment(sketch, "E51.12.18", {"start": v(24.44, 17.04) * mm, "end": v(25.02, 17.16) * mm});
            skLineSegment(sketch, "E51.12.19", {"start": v(24.15, 14.6) * mm, "end": v(24.37, 14.8) * mm});
            skLineSegment(sketch, "E51.12.20", {"start": v(23.96, 14.43) * mm, "end": v(24.15, 14.6) * mm});
            skLineSegment(sketch, "E51.12.21", {"start": v(23.15, 16.65) * mm, "end": v(23.51, 16.78) * mm});
            skLineSegment(sketch, "E51.12.22", {"start": v(22.87, 16.52) * mm, "end": v(23.15, 16.65) * mm});
            skLineSegment(sketch, "E51.12.23", {"start": v(22.5, 16.33) * mm, "end": v(22.65, 16.42) * mm});
            skLineSegment(sketch, "E51.12.24", {"start": v(23.71, 14.25) * mm, "end": v(23.74, 14.27) * mm});
            skLineSegment(sketch, "E51.12.25", {"start": v(23.74, 14.27) * mm, "end": v(23.83, 14.33) * mm});
            skLineSegment(sketch, "E51.12.26", {"start": v(22.65, 16.42) * mm, "end": v(22.87, 16.52) * mm});
            skLineSegment(sketch, "E51.12.27", {"start": v(23.83, 14.33) * mm, "end": v(23.96, 14.43) * mm});
            skLineSegment(sketch, "E51.12.28", {"start": v(22.4, 16.28) * mm, "end": v(22.5, 16.33) * mm});
            skLineSegment(sketch, "E51.12.29", {"start": v(22.38, 16.26) * mm, "end": v(22.4, 16.28) * mm});
            skLineSegment(sketch, "E51.13.0", {"start": v(15.72, 21.63) * mm, "end": v(16.26, 22.38) * mm});
            skLineSegment(sketch, "E51.13.1", {"start": v(19.57, 24.78) * mm, "end": v(19.68, 25.57) * mm});
            skLineSegment(sketch, "E51.13.2", {"start": v(17.54, 20.18) * mm, "end": v(18.15, 20.88) * mm});
            skLineSegment(sketch, "E51.13.3", {"start": v(19.43, 24.07) * mm, "end": v(19.57, 24.78) * mm});
            skLineSegment(sketch, "E51.13.4", {"start": v(19.08, 24.35) * mm, "end": v(19.74, 24.64) * mm});
            skLineSegment(sketch, "E51.13.5", {"start": v(19.74, 24.64) * mm, "end": v(20.48, 24.93) * mm});
            skLineSegment(sketch, "E51.13.6", {"start": v(19.27, 23.43) * mm, "end": v(19.43, 24.07) * mm});
            skLineSegment(sketch, "E51.13.7", {"start": v(19.76, 26.43) * mm, "end": v(19.8, 27.36) * mm});
            skLineSegment(sketch, "E51.13.8", {"start": v(19.1, 22.86) * mm, "end": v(19.27, 23.43) * mm});
            skLineSegment(sketch, "E51.13.9", {"start": v(21.3, 25.2) * mm, "end": v(22.2, 25.44) * mm});
            skLineSegment(sketch, "E51.13.10", {"start": v(19.68, 25.57) * mm, "end": v(19.76, 26.43) * mm});
            skLineSegment(sketch, "E51.13.11", {"start": v(18.5, 24.05) * mm, "end": v(19.08, 24.35) * mm});
            skLineSegment(sketch, "E51.13.12", {"start": v(20.48, 24.93) * mm, "end": v(21.3, 25.2) * mm});
            skLineSegment(sketch, "E51.13.13", {"start": v(18.6, 21.62) * mm, "end": v(18.76, 21.96) * mm});
            skLineSegment(sketch, "E51.13.14", {"start": v(18.76, 21.96) * mm, "end": v(18.93, 22.38) * mm});
            skLineSegment(sketch, "E51.13.15", {"start": v(18.93, 22.38) * mm, "end": v(19.1, 22.86) * mm});
            skLineSegment(sketch, "E51.13.16", {"start": v(17.54, 23.48) * mm, "end": v(17.98, 23.76) * mm});
            skLineSegment(sketch, "E51.13.17", {"start": v(17.18, 23.22) * mm, "end": v(17.54, 23.48) * mm});
            skLineSegment(sketch, "E51.13.18", {"start": v(17.98, 23.76) * mm, "end": v(18.5, 24.05) * mm});
            skLineSegment(sketch, "E51.13.19", {"start": v(18.45, 21.34) * mm, "end": v(18.6, 21.62) * mm});
            skLineSegment(sketch, "E51.13.20", {"start": v(18.33, 21.13) * mm, "end": v(18.45, 21.34) * mm});
            skLineSegment(sketch, "E51.13.21", {"start": v(16.88, 22.99) * mm, "end": v(17.18, 23.22) * mm});
            skLineSegment(sketch, "E51.13.22", {"start": v(16.64, 22.78) * mm, "end": v(16.88, 22.99) * mm});
            skLineSegment(sketch, "E51.13.23", {"start": v(16.35, 22.49) * mm, "end": v(16.47, 22.61) * mm});
            skLineSegment(sketch, "E51.13.24", {"start": v(18.15, 20.88) * mm, "end": v(18.17, 20.9) * mm});
            skLineSegment(sketch, "E51.13.25", {"start": v(18.17, 20.9) * mm, "end": v(18.23, 20.99) * mm});
            skLineSegment(sketch, "E51.13.26", {"start": v(16.47, 22.61) * mm, "end": v(16.64, 22.78) * mm});
            skLineSegment(sketch, "E51.13.27", {"start": v(18.23, 20.99) * mm, "end": v(18.33, 21.13) * mm});
            skLineSegment(sketch, "E51.13.28", {"start": v(16.28, 22.4) * mm, "end": v(16.35, 22.49) * mm});
            skLineSegment(sketch, "E51.13.29", {"start": v(16.26, 22.38) * mm, "end": v(16.28, 22.4) * mm});
            skLineSegment(sketch, "E51.14.0", {"start": v(8.26, 25.43) * mm, "end": v(8.55, 26.31) * mm});
            skLineSegment(sketch, "E51.14.1", {"start": v(10.95, 29.61) * mm, "end": v(10.82, 30.4) * mm});
            skLineSegment(sketch, "E51.14.2", {"start": v(10.45, 24.61) * mm, "end": v(10.8, 25.47) * mm});
            skLineSegment(sketch, "E51.14.3", {"start": v(11.04, 28.9) * mm, "end": v(10.95, 29.61) * mm});
            skLineSegment(sketch, "E51.14.4", {"start": v(10.62, 29.05) * mm, "end": v(11.16, 29.53) * mm});
            skLineSegment(sketch, "E51.14.5", {"start": v(11.16, 29.53) * mm, "end": v(11.78, 30.04) * mm});
            skLineSegment(sketch, "E51.14.6", {"start": v(11.1, 28.24) * mm, "end": v(11.04, 28.9) * mm});
            skLineSegment(sketch, "E51.14.7", {"start": v(10.62, 31.24) * mm, "end": v(10.37, 32.14) * mm});
            skLineSegment(sketch, "E51.14.8", {"start": v(11.1, 27.65) * mm, "end": v(11.1, 28.24) * mm});
            skLineSegment(sketch, "E51.14.9", {"start": v(12.48, 30.55) * mm, "end": v(13.26, 31.06) * mm});
            skLineSegment(sketch, "E51.14.10", {"start": v(10.82, 30.4) * mm, "end": v(10.62, 31.24) * mm});
            skLineSegment(sketch, "E51.14.11", {"start": v(10.15, 28.59) * mm, "end": v(10.62, 29.05) * mm});
            skLineSegment(sketch, "E51.14.12", {"start": v(11.78, 30.04) * mm, "end": v(12.48, 30.55) * mm});
            skLineSegment(sketch, "E51.14.13", {"start": v(11.01, 26.3) * mm, "end": v(11.06, 26.68) * mm});
            skLineSegment(sketch, "E51.14.14", {"start": v(11.06, 26.68) * mm, "end": v(11.1, 27.13) * mm});
            skLineSegment(sketch, "E51.14.15", {"start": v(11.1, 27.13) * mm, "end": v(11.1, 27.65) * mm});
            skLineSegment(sketch, "E51.14.16", {"start": v(9.43, 27.75) * mm, "end": v(9.76, 28.15) * mm});
            skLineSegment(sketch, "E51.14.17", {"start": v(9.16, 27.4) * mm, "end": v(9.43, 27.75) * mm});
            skLineSegment(sketch, "E51.14.18", {"start": v(9.76, 28.15) * mm, "end": v(10.15, 28.59) * mm});
            skLineSegment(sketch, "E51.14.19", {"start": v(10.96, 26) * mm, "end": v(11.01, 26.3) * mm});
            skLineSegment(sketch, "E51.14.20", {"start": v(10.9, 25.76) * mm, "end": v(10.96, 26) * mm});
            skLineSegment(sketch, "E51.14.21", {"start": v(8.95, 27.08) * mm, "end": v(9.16, 27.4) * mm});
            skLineSegment(sketch, "E51.14.22", {"start": v(8.79, 26.8) * mm, "end": v(8.95, 27.08) * mm});
            skLineSegment(sketch, "E51.14.23", {"start": v(8.6, 26.44) * mm, "end": v(8.67, 26.6) * mm});
            skLineSegment(sketch, "E51.14.24", {"start": v(10.8, 25.47) * mm, "end": v(10.82, 25.5) * mm});
            skLineSegment(sketch, "E51.14.25", {"start": v(10.82, 25.5) * mm, "end": v(10.85, 25.6) * mm});
            skLineSegment(sketch, "E51.14.26", {"start": v(8.67, 26.6) * mm, "end": v(8.79, 26.8) * mm});
            skLineSegment(sketch, "E51.14.27", {"start": v(10.85, 25.6) * mm, "end": v(10.9, 25.76) * mm});
            skLineSegment(sketch, "E51.14.28", {"start": v(8.56, 26.34) * mm, "end": v(8.6, 26.44) * mm});
            skLineSegment(sketch, "E51.14.29", {"start": v(8.55, 26.31) * mm, "end": v(8.56, 26.34) * mm});
            skLineSegment(sketch, "E51.15.0", {"start": v(0, 26.74) * mm, "end": v(0, 27.66) * mm});
            skLineSegment(sketch, "E51.15.1", {"start": v(1.27, 31.55) * mm, "end": v(0.9, 32.25) * mm});
            skLineSegment(sketch, "E51.15.2", {"start": v(2.33, 26.64) * mm, "end": v(2.41, 27.56) * mm});
            skLineSegment(sketch, "E51.15.3", {"start": v(1.57, 30.9) * mm, "end": v(1.27, 31.55) * mm});
            skLineSegment(sketch, "E51.15.4", {"start": v(1.12, 30.9) * mm, "end": v(1.49, 31.54) * mm});
            skLineSegment(sketch, "E51.15.5", {"start": v(1.49, 31.54) * mm, "end": v(1.92, 32.2) * mm});
            skLineSegment(sketch, "E51.15.6", {"start": v(1.82, 30.28) * mm, "end": v(1.57, 30.9) * mm});
            skLineSegment(sketch, "E51.15.7", {"start": v(0.45, 33) * mm, "end": v(-0.07, 33.77) * mm});
            skLineSegment(sketch, "E51.15.8", {"start": v(2.02, 29.73) * mm, "end": v(1.82, 30.28) * mm});
            skLineSegment(sketch, "E51.15.9", {"start": v(2.43, 32.9) * mm, "end": v(3.01, 33.63) * mm});
            skLineSegment(sketch, "E51.15.10", {"start": v(0.9, 32.25) * mm, "end": v(0.45, 33) * mm});
            skLineSegment(sketch, "E51.15.11", {"start": v(0.82, 30.33) * mm, "end": v(1.12, 30.9) * mm});
            skLineSegment(sketch, "E51.15.12", {"start": v(1.92, 32.2) * mm, "end": v(2.43, 32.9) * mm});
            skLineSegment(sketch, "E51.15.13", {"start": v(2.34, 28.42) * mm, "end": v(2.27, 28.8) * mm});
            skLineSegment(sketch, "E51.15.14", {"start": v(2.27, 28.8) * mm, "end": v(2.17, 29.23) * mm});
            skLineSegment(sketch, "E51.15.15", {"start": v(2.17, 29.23) * mm, "end": v(2.02, 29.73) * mm});
            skLineSegment(sketch, "E51.15.16", {"start": v(0.4, 29.3) * mm, "end": v(0.58, 29.8) * mm});
            skLineSegment(sketch, "E51.15.17", {"start": v(0.25, 28.88) * mm, "end": v(0.4, 29.3) * mm});
            skLineSegment(sketch, "E51.15.18", {"start": v(0.58, 29.8) * mm, "end": v(0.82, 30.33) * mm});
            skLineSegment(sketch, "E51.15.19", {"start": v(2.39, 28.11) * mm, "end": v(2.34, 28.42) * mm});
            skLineSegment(sketch, "E51.15.20", {"start": v(2.4, 27.87) * mm, "end": v(2.39, 28.11) * mm});
            skLineSegment(sketch, "E51.15.21", {"start": v(0.14, 28.52) * mm, "end": v(0.25, 28.88) * mm});
            skLineSegment(sketch, "E51.15.22", {"start": v(0.07, 28.21) * mm, "end": v(0.14, 28.52) * mm});
            skLineSegment(sketch, "E51.15.23", {"start": v(0, 27.8) * mm, "end": v(0.03, 27.97) * mm});
            skLineSegment(sketch, "E51.15.24", {"start": v(2.41, 27.56) * mm, "end": v(2.41, 27.6) * mm});
            skLineSegment(sketch, "E51.15.25", {"start": v(2.41, 27.6) * mm, "end": v(2.41, 27.7) * mm});
            skLineSegment(sketch, "E51.15.26", {"start": v(0.03, 27.97) * mm, "end": v(0.07, 28.21) * mm});
            skLineSegment(sketch, "E51.15.27", {"start": v(2.41, 27.7) * mm, "end": v(2.4, 27.87) * mm});
            skLineSegment(sketch, "E51.15.28", {"start": v(0, 27.7) * mm, "end": v(0, 27.8) * mm});
            skLineSegment(sketch, "E51.15.29", {"start": v(0, 27.66) * mm, "end": v(0, 27.7) * mm});
            skLineSegment(sketch, "E51.16.0", {"start": v(-8.26, 25.43) * mm, "end": v(-8.55, 26.31) * mm});
            skLineSegment(sketch, "E51.16.1", {"start": v(-8.54, 30.4) * mm, "end": v(-9.12, 30.95) * mm});
            skLineSegment(sketch, "E51.16.2", {"start": v(-6.01, 26.05) * mm, "end": v(-6.22, 26.96) * mm});
            skLineSegment(sketch, "E51.16.3", {"start": v(-8.05, 29.86) * mm, "end": v(-8.54, 30.4) * mm});
            skLineSegment(sketch, "E51.16.4", {"start": v(-8.48, 29.74) * mm, "end": v(-8.33, 30.45) * mm});
            skLineSegment(sketch, "E51.16.5", {"start": v(-8.33, 30.45) * mm, "end": v(-8.12, 31.22) * mm});
            skLineSegment(sketch, "E51.16.6", {"start": v(-7.62, 29.36) * mm, "end": v(-8.05, 29.86) * mm});
            skLineSegment(sketch, "E51.16.7", {"start": v(-9.77, 31.52) * mm, "end": v(-10.5, 32.1) * mm});
            skLineSegment(sketch, "E51.16.8", {"start": v(-7.27, 28.9) * mm, "end": v(-7.62, 29.36) * mm});
            skLineSegment(sketch, "E51.16.9", {"start": v(-7.86, 32.05) * mm, "end": v(-7.53, 32.92) * mm});
            skLineSegment(sketch, "E51.16.10", {"start": v(-9.12, 30.95) * mm, "end": v(-9.77, 31.52) * mm});
            skLineSegment(sketch, "E51.16.11", {"start": v(-8.59, 29.1) * mm, "end": v(-8.48, 29.74) * mm});
            skLineSegment(sketch, "E51.16.12", {"start": v(-8.12, 31.22) * mm, "end": v(-7.86, 32.05) * mm});
            skLineSegment(sketch, "E51.16.13", {"start": v(-6.55, 27.75) * mm, "end": v(-6.74, 28.09) * mm});
            skLineSegment(sketch, "E51.16.14", {"start": v(-6.74, 28.09) * mm, "end": v(-6.97, 28.47) * mm});
            skLineSegment(sketch, "E51.16.15", {"start": v(-6.97, 28.47) * mm, "end": v(-7.27, 28.9) * mm});
            skLineSegment(sketch, "E51.16.16", {"start": v(-8.69, 28) * mm, "end": v(-8.65, 28.51) * mm});
            skLineSegment(sketch, "E51.16.17", {"start": v(-8.7, 27.54) * mm, "end": v(-8.69, 28) * mm});
            skLineSegment(sketch, "E51.16.18", {"start": v(-8.65, 28.51) * mm, "end": v(-8.59, 29.1) * mm});
            skLineSegment(sketch, "E51.16.19", {"start": v(-6.42, 27.47) * mm, "end": v(-6.55, 27.75) * mm});
            skLineSegment(sketch, "E51.16.20", {"start": v(-6.32, 27.25) * mm, "end": v(-6.42, 27.47) * mm});
            skLineSegment(sketch, "E51.16.21", {"start": v(-8.68, 27.16) * mm, "end": v(-8.7, 27.54) * mm});
            skLineSegment(sketch, "E51.16.22", {"start": v(-8.65, 26.85) * mm, "end": v(-8.68, 27.16) * mm});
            skLineSegment(sketch, "E51.16.23", {"start": v(-8.58, 26.44) * mm, "end": v(-8.62, 26.61) * mm});
            skLineSegment(sketch, "E51.16.24", {"start": v(-6.22, 26.96) * mm, "end": v(-6.23, 26.99) * mm});
            skLineSegment(sketch, "E51.16.25", {"start": v(-6.23, 26.99) * mm, "end": v(-6.26, 27.09) * mm});
            skLineSegment(sketch, "E51.16.26", {"start": v(-8.62, 26.61) * mm, "end": v(-8.65, 26.85) * mm});
            skLineSegment(sketch, "E51.16.27", {"start": v(-6.26, 27.09) * mm, "end": v(-6.32, 27.25) * mm});
            skLineSegment(sketch, "E51.16.28", {"start": v(-8.56, 26.34) * mm, "end": v(-8.58, 26.44) * mm});
            skLineSegment(sketch, "E51.16.29", {"start": v(-8.55, 26.31) * mm, "end": v(-8.56, 26.34) * mm});
            skLineSegment(sketch, "E51.17.0", {"start": v(-15.72, 21.63) * mm, "end": v(-16.26, 22.38) * mm});
            skLineSegment(sketch, "E51.17.1", {"start": v(-17.52, 26.27) * mm, "end": v(-18.23, 26.62) * mm});
            skLineSegment(sketch, "E51.17.2", {"start": v(-13.77, 22.92) * mm, "end": v(-14.25, 23.71) * mm});
            skLineSegment(sketch, "E51.17.3", {"start": v(-16.88, 25.92) * mm, "end": v(-17.52, 26.27) * mm});
            skLineSegment(sketch, "E51.17.4", {"start": v(-17.26, 25.67) * mm, "end": v(-17.33, 26.39) * mm});
            skLineSegment(sketch, "E51.17.5", {"start": v(-17.33, 26.39) * mm, "end": v(-17.38, 27.18) * mm});
            skLineSegment(sketch, "E51.17.6", {"start": v(-16.32, 25.57) * mm, "end": v(-16.88, 25.92) * mm});
            skLineSegment(sketch, "E51.17.7", {"start": v(-19.03, 26.96) * mm, "end": v(-19.9, 27.28) * mm});
            skLineSegment(sketch, "E51.17.8", {"start": v(-15.84, 25.24) * mm, "end": v(-16.32, 25.57) * mm});
            skLineSegment(sketch, "E51.17.9", {"start": v(-17.38, 28.05) * mm, "end": v(-17.33, 28.98) * mm});
            skLineSegment(sketch, "E51.17.10", {"start": v(-18.23, 26.62) * mm, "end": v(-19.03, 26.96) * mm});
            skLineSegment(sketch, "E51.17.11", {"start": v(-17.16, 25.02) * mm, "end": v(-17.26, 25.67) * mm});
            skLineSegment(sketch, "E51.17.12", {"start": v(-17.38, 27.18) * mm, "end": v(-17.38, 28.05) * mm});
            skLineSegment(sketch, "E51.17.13", {"start": v(-14.8, 24.37) * mm, "end": v(-15.09, 24.63) * mm});
            skLineSegment(sketch, "E51.17.14", {"start": v(-15.09, 24.63) * mm, "end": v(-15.43, 24.92) * mm});
            skLineSegment(sketch, "E51.17.15", {"start": v(-15.43, 24.92) * mm, "end": v(-15.84, 25.24) * mm});
            skLineSegment(sketch, "E51.17.16", {"start": v(-16.91, 23.94) * mm, "end": v(-17.04, 24.44) * mm});
            skLineSegment(sketch, "E51.17.17", {"start": v(-16.78, 23.51) * mm, "end": v(-16.91, 23.94) * mm});
            skLineSegment(sketch, "E51.17.18", {"start": v(-17.04, 24.44) * mm, "end": v(-17.16, 25.02) * mm});
            skLineSegment(sketch, "E51.17.19", {"start": v(-14.6, 24.15) * mm, "end": v(-14.8, 24.37) * mm});
            skLineSegment(sketch, "E51.17.20", {"start": v(-14.43, 23.96) * mm, "end": v(-14.6, 24.15) * mm});
            skLineSegment(sketch, "E51.17.21", {"start": v(-16.65, 23.15) * mm, "end": v(-16.78, 23.51) * mm});
            skLineSegment(sketch, "E51.17.22", {"start": v(-16.52, 22.87) * mm, "end": v(-16.65, 23.15) * mm});
            skLineSegment(sketch, "E51.17.23", {"start": v(-16.33, 22.5) * mm, "end": v(-16.42, 22.65) * mm});
            skLineSegment(sketch, "E51.17.24", {"start": v(-14.25, 23.71) * mm, "end": v(-14.27, 23.74) * mm});
            skLineSegment(sketch, "E51.17.25", {"start": v(-14.27, 23.74) * mm, "end": v(-14.33, 23.83) * mm});
            skLineSegment(sketch, "E51.17.26", {"start": v(-16.42, 22.65) * mm, "end": v(-16.52, 22.87) * mm});
            skLineSegment(sketch, "E51.17.27", {"start": v(-14.33, 23.83) * mm, "end": v(-14.43, 23.96) * mm});
            skLineSegment(sketch, "E51.17.28", {"start": v(-16.28, 22.4) * mm, "end": v(-16.33, 22.5) * mm});
            skLineSegment(sketch, "E51.17.29", {"start": v(-16.26, 22.38) * mm, "end": v(-16.28, 22.4) * mm});
            skLineSegment(sketch, "E51.18.0", {"start": v(-21.63, 15.72) * mm, "end": v(-22.38, 16.26) * mm});
            skLineSegment(sketch, "E51.18.1", {"start": v(-24.78, 19.57) * mm, "end": v(-25.57, 19.68) * mm});
            skLineSegment(sketch, "E51.18.2", {"start": v(-20.18, 17.54) * mm, "end": v(-20.88, 18.15) * mm});
            skLineSegment(sketch, "E51.18.3", {"start": v(-24.07, 19.43) * mm, "end": v(-24.78, 19.57) * mm});
            skLineSegment(sketch, "E51.18.4", {"start": v(-24.35, 19.08) * mm, "end": v(-24.64, 19.74) * mm});
            skLineSegment(sketch, "E51.18.5", {"start": v(-24.64, 19.74) * mm, "end": v(-24.93, 20.48) * mm});
            skLineSegment(sketch, "E51.18.6", {"start": v(-23.43, 19.27) * mm, "end": v(-24.07, 19.43) * mm});
            skLineSegment(sketch, "E51.18.7", {"start": v(-26.43, 19.76) * mm, "end": v(-27.36, 19.8) * mm});
            skLineSegment(sketch, "E51.18.8", {"start": v(-22.86, 19.1) * mm, "end": v(-23.43, 19.27) * mm});
            skLineSegment(sketch, "E51.18.9", {"start": v(-25.2, 21.3) * mm, "end": v(-25.44, 22.2) * mm});
            skLineSegment(sketch, "E51.18.10", {"start": v(-25.57, 19.68) * mm, "end": v(-26.43, 19.76) * mm});
            skLineSegment(sketch, "E51.18.11", {"start": v(-24.05, 18.5) * mm, "end": v(-24.35, 19.08) * mm});
            skLineSegment(sketch, "E51.18.12", {"start": v(-24.93, 20.48) * mm, "end": v(-25.2, 21.3) * mm});
            skLineSegment(sketch, "E51.18.13", {"start": v(-21.62, 18.6) * mm, "end": v(-21.96, 18.76) * mm});
            skLineSegment(sketch, "E51.18.14", {"start": v(-21.96, 18.76) * mm, "end": v(-22.38, 18.93) * mm});
            skLineSegment(sketch, "E51.18.15", {"start": v(-22.38, 18.93) * mm, "end": v(-22.86, 19.1) * mm});
            skLineSegment(sketch, "E51.18.16", {"start": v(-23.48, 17.54) * mm, "end": v(-23.76, 17.98) * mm});
            skLineSegment(sketch, "E51.18.17", {"start": v(-23.22, 17.18) * mm, "end": v(-23.48, 17.54) * mm});
            skLineSegment(sketch, "E51.18.18", {"start": v(-23.76, 17.98) * mm, "end": v(-24.05, 18.5) * mm});
            skLineSegment(sketch, "E51.18.19", {"start": v(-21.34, 18.45) * mm, "end": v(-21.62, 18.6) * mm});
            skLineSegment(sketch, "E51.18.20", {"start": v(-21.13, 18.33) * mm, "end": v(-21.34, 18.45) * mm});
            skLineSegment(sketch, "E51.18.21", {"start": v(-22.99, 16.88) * mm, "end": v(-23.22, 17.18) * mm});
            skLineSegment(sketch, "E51.18.22", {"start": v(-22.78, 16.64) * mm, "end": v(-22.99, 16.88) * mm});
            skLineSegment(sketch, "E51.18.23", {"start": v(-22.49, 16.35) * mm, "end": v(-22.61, 16.47) * mm});
            skLineSegment(sketch, "E51.18.24", {"start": v(-20.88, 18.15) * mm, "end": v(-20.9, 18.17) * mm});
            skLineSegment(sketch, "E51.18.25", {"start": v(-20.9, 18.17) * mm, "end": v(-20.99, 18.23) * mm});
            skLineSegment(sketch, "E51.18.26", {"start": v(-22.61, 16.47) * mm, "end": v(-22.78, 16.64) * mm});
            skLineSegment(sketch, "E51.18.27", {"start": v(-20.99, 18.23) * mm, "end": v(-21.13, 18.33) * mm});
            skLineSegment(sketch, "E51.18.28", {"start": v(-22.4, 16.28) * mm, "end": v(-22.49, 16.35) * mm});
            skLineSegment(sketch, "E51.18.29", {"start": v(-22.38, 16.26) * mm, "end": v(-22.4, 16.28) * mm});
            skLineSegment(sketch, "E51.19.0", {"start": v(-25.43, 8.26) * mm, "end": v(-26.31, 8.55) * mm});
            skLineSegment(sketch, "E51.19.1", {"start": v(-29.61, 10.95) * mm, "end": v(-30.4, 10.82) * mm});
            skLineSegment(sketch, "E51.19.2", {"start": v(-24.61, 10.45) * mm, "end": v(-25.47, 10.8) * mm});
            skLineSegment(sketch, "E51.19.3", {"start": v(-28.9, 11.04) * mm, "end": v(-29.61, 10.95) * mm});
            skLineSegment(sketch, "E51.19.4", {"start": v(-29.05, 10.62) * mm, "end": v(-29.53, 11.16) * mm});
            skLineSegment(sketch, "E51.19.5", {"start": v(-29.53, 11.16) * mm, "end": v(-30.04, 11.78) * mm});
            skLineSegment(sketch, "E51.19.6", {"start": v(-28.24, 11.1) * mm, "end": v(-28.9, 11.04) * mm});
            skLineSegment(sketch, "E51.19.7", {"start": v(-31.24, 10.62) * mm, "end": v(-32.14, 10.37) * mm});
            skLineSegment(sketch, "E51.19.8", {"start": v(-27.65, 11.1) * mm, "end": v(-28.24, 11.1) * mm});
            skLineSegment(sketch, "E51.19.9", {"start": v(-30.55, 12.48) * mm, "end": v(-31.06, 13.26) * mm});
            skLineSegment(sketch, "E51.19.10", {"start": v(-30.4, 10.82) * mm, "end": v(-31.24, 10.62) * mm});
            skLineSegment(sketch, "E51.19.11", {"start": v(-28.59, 10.15) * mm, "end": v(-29.05, 10.62) * mm});
            skLineSegment(sketch, "E51.19.12", {"start": v(-30.04, 11.78) * mm, "end": v(-30.55, 12.48) * mm});
            skLineSegment(sketch, "E51.19.13", {"start": v(-26.3, 11.01) * mm, "end": v(-26.68, 11.06) * mm});
            skLineSegment(sketch, "E51.19.14", {"start": v(-26.68, 11.06) * mm, "end": v(-27.13, 11.1) * mm});
            skLineSegment(sketch, "E51.19.15", {"start": v(-27.13, 11.1) * mm, "end": v(-27.65, 11.1) * mm});
            skLineSegment(sketch, "E51.19.16", {"start": v(-27.75, 9.43) * mm, "end": v(-28.15, 9.76) * mm});
            skLineSegment(sketch, "E51.19.17", {"start": v(-27.4, 9.16) * mm, "end": v(-27.75, 9.43) * mm});
            skLineSegment(sketch, "E51.19.18", {"start": v(-28.15, 9.76) * mm, "end": v(-28.59, 10.15) * mm});
            skLineSegment(sketch, "E51.19.19", {"start": v(-26, 10.96) * mm, "end": v(-26.3, 11.01) * mm});
            skLineSegment(sketch, "E51.19.20", {"start": v(-25.76, 10.9) * mm, "end": v(-26, 10.96) * mm});
            skLineSegment(sketch, "E51.19.21", {"start": v(-27.08, 8.95) * mm, "end": v(-27.4, 9.16) * mm});
            skLineSegment(sketch, "E51.19.22", {"start": v(-26.8, 8.79) * mm, "end": v(-27.08, 8.95) * mm});
            skLineSegment(sketch, "E51.19.23", {"start": v(-26.44, 8.6) * mm, "end": v(-26.6, 8.67) * mm});
            skLineSegment(sketch, "E51.19.24", {"start": v(-25.47, 10.8) * mm, "end": v(-25.5, 10.82) * mm});
            skLineSegment(sketch, "E51.19.25", {"start": v(-25.5, 10.82) * mm, "end": v(-25.6, 10.85) * mm});
            skLineSegment(sketch, "E51.19.26", {"start": v(-26.6, 8.67) * mm, "end": v(-26.8, 8.79) * mm});
            skLineSegment(sketch, "E51.19.27", {"start": v(-25.6, 10.85) * mm, "end": v(-25.76, 10.9) * mm});
            skLineSegment(sketch, "E51.19.28", {"start": v(-26.34, 8.56) * mm, "end": v(-26.44, 8.6) * mm});
            skLineSegment(sketch, "E51.19.29", {"start": v(-26.31, 8.55) * mm, "end": v(-26.34, 8.56) * mm});
            skSolve(sketch);
        }
        {
            var Q0;
            {var subQ0=sQuery(id+"F1.wireOp",EDGE,"E0");var subQ27=makeQuery(id+"F1.imprint","INTERSECT",VERTEX,{"derivedFrom":[subQ0,sQuery(id+"F1.wireOp",EDGE,"E51.10.0")]});Q0=makeQuery(id+"F1.imprint","IMPRINT",FACE,{"disambiguationData":[TD([[makeQuery(id+"F1.imprint","IMPRINT",EDGE,{"disambiguationData":[TD([[subQ27,-1.0]])],"derivedFrom":subQ0}),1.0]])]});}
            var Q1;
            {var subQ0=sQuery(id+"F1.wireOp",EDGE,"E51.1.0");Q1=makeQuery(id+"F1.imprint","IMPRINT",FACE,{"disambiguationData":[TD([[makeQuery(id+"F1.imprint","IMPRINT",EDGE,{"derivedFrom":subQ0}),-1.0]])]});}
            var Q2;
            {var subQ7=sQuery(id+"F1.wireOp",EDGE,"E51.2.0");Q2=makeQuery(id+"F1.imprint","IMPRINT",FACE,{"disambiguationData":[TD([[makeQuery(id+"F1.imprint","IMPRINT",EDGE,{"derivedFrom":subQ7}),-1.0]])]});}
            var Q3;
            {var subQ8=sQuery(id+"F1.wireOp",EDGE,"E51.3.0");Q3=makeQuery(id+"F1.imprint","IMPRINT",FACE,{"disambiguationData":[TD([[makeQuery(id+"F1.imprint","IMPRINT",EDGE,{"derivedFrom":subQ8}),-1.0]])]});}
            var Q4;
            {var subQ2=sQuery(id+"F1.wireOp",EDGE,"E51.4.0");Q4=makeQuery(id+"F1.imprint","IMPRINT",FACE,{"disambiguationData":[TD([[makeQuery(id+"F1.imprint","IMPRINT",EDGE,{"derivedFrom":subQ2}),-1.0]])]});}
            var Q5;
            {var subQ8=sQuery(id+"F1.wireOp",EDGE,"E51.5.0");Q5=makeQuery(id+"F1.imprint","IMPRINT",FACE,{"disambiguationData":[TD([[makeQuery(id+"F1.imprint","IMPRINT",EDGE,{"derivedFrom":subQ8}),-1.0]])]});}
            var Q6;
            {var subQ3=sQuery(id+"F1.wireOp",EDGE,"E51.6.0");Q6=makeQuery(id+"F1.imprint","IMPRINT",FACE,{"disambiguationData":[TD([[makeQuery(id+"F1.imprint","IMPRINT",EDGE,{"derivedFrom":subQ3}),-1.0]])]});}
            var Q7;
            {var subQ0=sQuery(id+"F1.wireOp",EDGE,"E51.7.0");Q7=makeQuery(id+"F1.imprint","IMPRINT",FACE,{"disambiguationData":[TD([[makeQuery(id+"F1.imprint","IMPRINT",EDGE,{"derivedFrom":subQ0}),-1.0]])]});}
            var Q8;
            {var subQ5=sQuery(id+"F1.wireOp",EDGE,"E51.8.0");Q8=makeQuery(id+"F1.imprint","IMPRINT",FACE,{"disambiguationData":[TD([[makeQuery(id+"F1.imprint","IMPRINT",EDGE,{"derivedFrom":subQ5}),-1.0]])]});}
            var Q9;
            {var subQ1=sQuery(id+"F1.wireOp",EDGE,"E51.9.0");Q9=makeQuery(id+"F1.imprint","IMPRINT",FACE,{"disambiguationData":[TD([[makeQuery(id+"F1.imprint","IMPRINT",EDGE,{"derivedFrom":subQ1}),-1.0]])]});}
            var Q10;
            {var subQ5=sQuery(id+"F1.wireOp",EDGE,"E51.10.0");Q10=makeQuery(id+"F1.imprint","IMPRINT",FACE,{"disambiguationData":[TD([[makeQuery(id+"F1.imprint","IMPRINT",EDGE,{"derivedFrom":subQ5}),-1.0]])]});}
            var Q11;
            {var subQ8=sQuery(id+"F1.wireOp",EDGE,"E51.11.0");Q11=makeQuery(id+"F1.imprint","IMPRINT",FACE,{"disambiguationData":[TD([[makeQuery(id+"F1.imprint","IMPRINT",EDGE,{"derivedFrom":subQ8}),-1.0]])]});}
            var Q12;
            {var subQ2=sQuery(id+"F1.wireOp",EDGE,"E51.12.0");Q12=makeQuery(id+"F1.imprint","IMPRINT",FACE,{"disambiguationData":[TD([[makeQuery(id+"F1.imprint","IMPRINT",EDGE,{"derivedFrom":subQ2}),-1.0]])]});}
            var Q13;
            {var subQ3=sQuery(id+"F1.wireOp",EDGE,"E51.13.0");Q13=makeQuery(id+"F1.imprint","IMPRINT",FACE,{"disambiguationData":[TD([[makeQuery(id+"F1.imprint","IMPRINT",EDGE,{"derivedFrom":subQ3}),-1.0]])]});}
            var Q14;
            {var subQ0=sQuery(id+"F1.wireOp",EDGE,"E51.14.0");Q14=makeQuery(id+"F1.imprint","IMPRINT",FACE,{"disambiguationData":[TD([[makeQuery(id+"F1.imprint","IMPRINT",EDGE,{"derivedFrom":subQ0}),-1.0]])]});}
            var Q15;
            {var subQ6=sQuery(id+"F1.wireOp",EDGE,"E51.15.0");Q15=makeQuery(id+"F1.imprint","IMPRINT",FACE,{"disambiguationData":[TD([[makeQuery(id+"F1.imprint","IMPRINT",EDGE,{"derivedFrom":subQ6}),-1.0]])]});}
            var Q16;
            {var subQ5=sQuery(id+"F1.wireOp",EDGE,"E51.16.0");Q16=makeQuery(id+"F1.imprint","IMPRINT",FACE,{"disambiguationData":[TD([[makeQuery(id+"F1.imprint","IMPRINT",EDGE,{"derivedFrom":subQ5}),-1.0]])]});}
            var Q17;
            {var subQ7=sQuery(id+"F1.wireOp",EDGE,"E51.17.0");Q17=makeQuery(id+"F1.imprint","IMPRINT",FACE,{"disambiguationData":[TD([[makeQuery(id+"F1.imprint","IMPRINT",EDGE,{"derivedFrom":subQ7}),-1.0]])]});}
            var Q18;
            {var subQ5=sQuery(id+"F1.wireOp",EDGE,"E51.18.0");Q18=makeQuery(id+"F1.imprint","IMPRINT",FACE,{"disambiguationData":[TD([[makeQuery(id+"F1.imprint","IMPRINT",EDGE,{"derivedFrom":subQ5}),-1.0]])]});}
            var Q19;
            {var subQ8=sQuery(id+"F1.wireOp",EDGE,"E51.19.0");Q19=makeQuery(id+"F1.imprint","IMPRINT",FACE,{"disambiguationData":[TD([[makeQuery(id+"F1.imprint","IMPRINT",EDGE,{"derivedFrom":subQ8}),-1.0]])]});}
            var Q20;
            {var subQ8=sQuery(id+"F1.wireOp",EDGE,"E21");Q20=makeQuery(id+"F1.imprint","IMPRINT",FACE,{"disambiguationData":[TD([[makeQuery(id+"F1.imprint","IMPRINT",EDGE,{"derivedFrom":subQ8}),-1.0]])]});}
            extrude(context, id + "F2", {"entities" : qUnion([Q0, Q1, Q2, Q3, Q4, Q5, Q6, Q7, Q8, Q9, Q10, Q11, Q12, Q13, Q14, Q15, Q16, Q17, Q18, Q19, Q20]), "depth" : (getVariable(context, 'GearThickness')) * mm});
        }
    });
